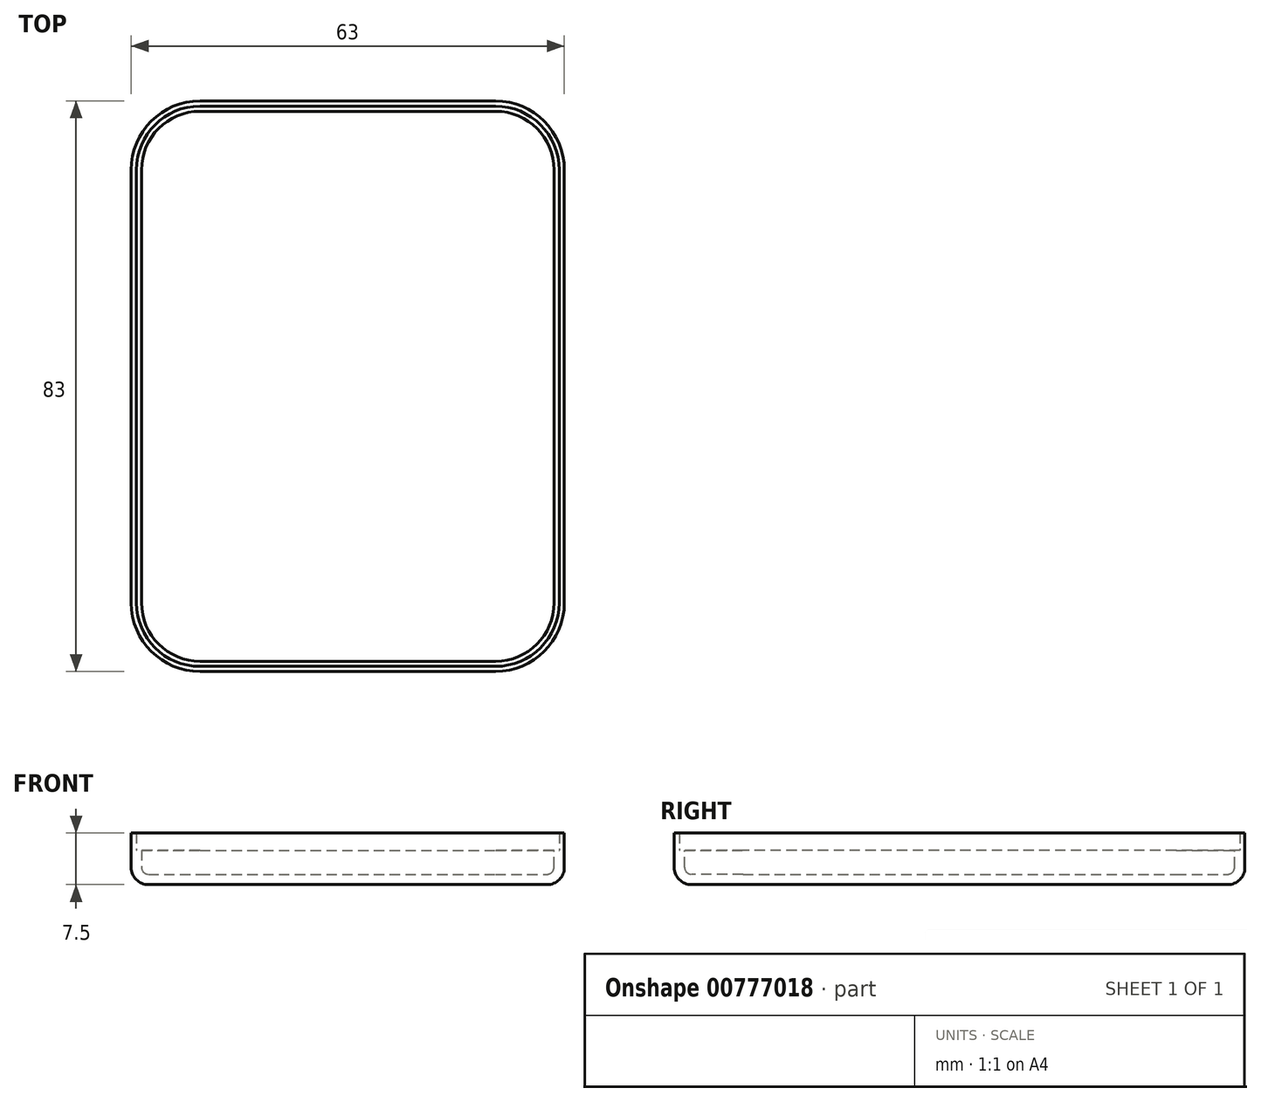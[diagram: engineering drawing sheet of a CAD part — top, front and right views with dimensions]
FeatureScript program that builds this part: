
annotation { "Feature Type Name" : "Feature", "Feature Type Description" : "" }
export const myFeature = defineFeature(function(context is Context, id is Id, definition is map)
    precondition{}
    {
        {
            var Q0;
            Q0=qCreatedBy(makeId("Top.planeOp"),FACE);
            var sketch = newSketch(context, id + "F0", { "sketchPlane" : qUnion([Q0])});
            skLineSegment(sketch, "E0.bottom", {"start": v(-59.26, 55.44) * mm, "end": v(-16.26, 55.44) * mm});
            skLineSegment(sketch, "E0.top", {"start": v(-59.26, -27.56) * mm, "end": v(-16.26, -27.56) * mm});
            skLineSegment(sketch, "E0.left", {"start": v(-69.26, 45.44) * mm, "end": v(-69.26, -17.56) * mm});
            skLineSegment(sketch, "E0.right", {"start": v(-6.26, 45.44) * mm, "end": v(-6.26, -17.56) * mm});
            skPoint(sketch, "E1.visualSharp", {"position": v(-69.26, 55.44) * mm});
            skArc(sketch, "E1.filletArc", {"start": v(-59.26, 55.44) * mm, "mid": v(-66.33, 52.5) * mm, "end": v(-69.26, 45.44) * mm});
            skPoint(sketch, "E2.visualSharp", {"position": v(-6.26, 55.44) * mm});
            skArc(sketch, "E2.filletArc", {"start": v(-6.26, 45.44) * mm, "mid": v(-9.19, 52.5) * mm, "end": v(-16.26, 55.44) * mm});
            skPoint(sketch, "E3.visualSharp", {"position": v(-6.26, -27.56) * mm});
            skArc(sketch, "E3.filletArc", {"start": v(-16.26, -27.56) * mm, "mid": v(-9.19, -24.63) * mm, "end": v(-6.26, -17.56) * mm});
            skPoint(sketch, "E4.visualSharp", {"position": v(-69.26, -27.56) * mm});
            skArc(sketch, "E4.filletArc", {"start": v(-69.26, -17.56) * mm, "mid": v(-66.33, -24.63) * mm, "end": v(-59.26, -27.56) * mm});
            skSolve(sketch);
        }
        {
            var Q0;
            Q0=qSketchRegion(id+"F0",true);
            extrude(context, id + "F1", {"entities" : qUnion([Q0]), "flatOperationType" : FlatOperationType.REMOVE, "depth" : 5 * mm, "offsetDistance" : 25 * mm, "domain" : OperationDomain.MODEL});
        }
        {
            var Q0;
            Q0=makeQuery(id+"F1.opExtrude","CAP_FACE",FACE,{"disambiguationData":[OSD([sQuery(id+"F0.wireOp",EDGE,"E0.bottom"),sQuery(id+"F0.wireOp",EDGE,"E0.top"),sQuery(id+"F0.wireOp",EDGE,"E0.left"),sQuery(id+"F0.wireOp",EDGE,"E0.right"),sQuery(id+"F0.wireOp",EDGE,"E1.filletArc"),sQuery(id+"F0.wireOp",EDGE,"E2.filletArc"),sQuery(id+"F0.wireOp",EDGE,"E3.filletArc"),sQuery(id+"F0.wireOp",EDGE,"E4.filletArc")])],"isStart":true});
            fillet(context, id + "F2", {"entities" : qUnion([Q0]), "radius" : 2.5 * mm, "tangentPropagation" : true, "allowEdgeOverflow" : false});
        }
        {
            var Q0;
            Q0=makeQuery(id+"F1.opExtrude","CAP_FACE",FACE,{"disambiguationData":[OSD([sQuery(id+"F0.wireOp",EDGE,"E0.bottom"),sQuery(id+"F0.wireOp",EDGE,"E0.top"),sQuery(id+"F0.wireOp",EDGE,"E0.left"),sQuery(id+"F0.wireOp",EDGE,"E0.right"),sQuery(id+"F0.wireOp",EDGE,"E1.filletArc"),sQuery(id+"F0.wireOp",EDGE,"E2.filletArc"),sQuery(id+"F0.wireOp",EDGE,"E3.filletArc"),sQuery(id+"F0.wireOp",EDGE,"E4.filletArc")])],"isStart":false});
            shell(context, id + "F3", {"entities" : qUnion([Q0]), "thickness" : 1.5 * mm});
        }
        {
            var Q0;
            Q0=makeQuery(id+"F1.opExtrude","CAP_FACE",FACE,{"disambiguationData":[OSD([sQuery(id+"F0.wireOp",EDGE,"E0.bottom"),sQuery(id+"F0.wireOp",EDGE,"E0.left"),sQuery(id+"F0.wireOp",EDGE,"E0.right"),sQuery(id+"F0.wireOp",EDGE,"E1.filletArc"),sQuery(id+"F0.wireOp",EDGE,"E2.filletArc"),sQuery(id+"F0.wireOp",EDGE,"E3.filletArc"),sQuery(id+"F0.wireOp",EDGE,"E4.filletArc"),sQuery(id+"F0.wireOp",EDGE,"d9edf215-bd34-4b25-a5de-3ec3039a00d7.direction1")])],"isStart":false});
            var sketch = newSketch(context, id + "F4", { "sketchPlane" : qUnion([Q0])});
            skArc(sketch, "E5.0", {"start": v(-16.26, -27.56) * mm, "mid": v(-9.19, -24.63) * mm, "end": v(-6.26, -17.56) * mm});
            skLineSegment(sketch, "E5.1", {"start": v(-6.26, 45.44) * mm, "end": v(-6.26, -17.56) * mm});
            skArc(sketch, "E5.2", {"start": v(-6.26, 45.44) * mm, "mid": v(-9.19, 52.5) * mm, "end": v(-16.26, 55.44) * mm});
            skLineSegment(sketch, "E5.3", {"start": v(-59.26, 55.44) * mm, "end": v(-16.26, 55.44) * mm});
            skArc(sketch, "E5.4", {"start": v(-59.26, 55.44) * mm, "mid": v(-66.33, 52.5) * mm, "end": v(-69.26, 45.44) * mm});
            skLineSegment(sketch, "E5.5", {"start": v(-69.26, 45.44) * mm, "end": v(-69.26, -17.56) * mm});
            skArc(sketch, "E5.6", {"start": v(-69.26, -17.56) * mm, "mid": v(-66.33, -24.63) * mm, "end": v(-59.26, -27.56) * mm});
            skLineSegment(sketch, "E5.7", {"start": v(-59.26, -27.56) * mm, "end": v(-16.26, -27.56) * mm});
            skArc(sketch, "E6.0", {"start": v(-59.26, 54.69) * mm, "mid": v(-65.8, 51.98) * mm, "end": v(-68.5, 45.44) * mm});
            skLineSegment(sketch, "E6.1", {"start": v(-68.5, 45.44) * mm, "end": v(-68.5, -17.56) * mm});
            skLineSegment(sketch, "E6.2", {"start": v(-59.26, 54.69) * mm, "end": v(-16.26, 54.69) * mm});
            skArc(sketch, "E6.3", {"start": v(-68.5, -17.56) * mm, "mid": v(-65.8, -24.1) * mm, "end": v(-59.26, -26.81) * mm});
            skArc(sketch, "E6.4", {"start": v(-7, 45.44) * mm, "mid": v(-9.72, 51.98) * mm, "end": v(-16.26, 54.69) * mm});
            skLineSegment(sketch, "E6.5", {"start": v(-7, 45.44) * mm, "end": v(-7, -17.56) * mm});
            skArc(sketch, "E6.6", {"start": v(-16.26, -26.81) * mm, "mid": v(-9.72, -24.1) * mm, "end": v(-7, -17.56) * mm});
            skLineSegment(sketch, "E6.7", {"start": v(-59.26, -26.81) * mm, "end": v(-16.26, -26.81) * mm});
            skSolve(sketch);
        }
        {
            var Q0;
            Q0 = qSketchRegion(id + "F4", true);
            extrude(context, id + "F5", {"entities" : qUnion([Q0]), "operationType" : NewBodyOperationType.ADD, "depth" : 2.5 * mm, "offsetDistance" : 25 * mm});
        }
    });
